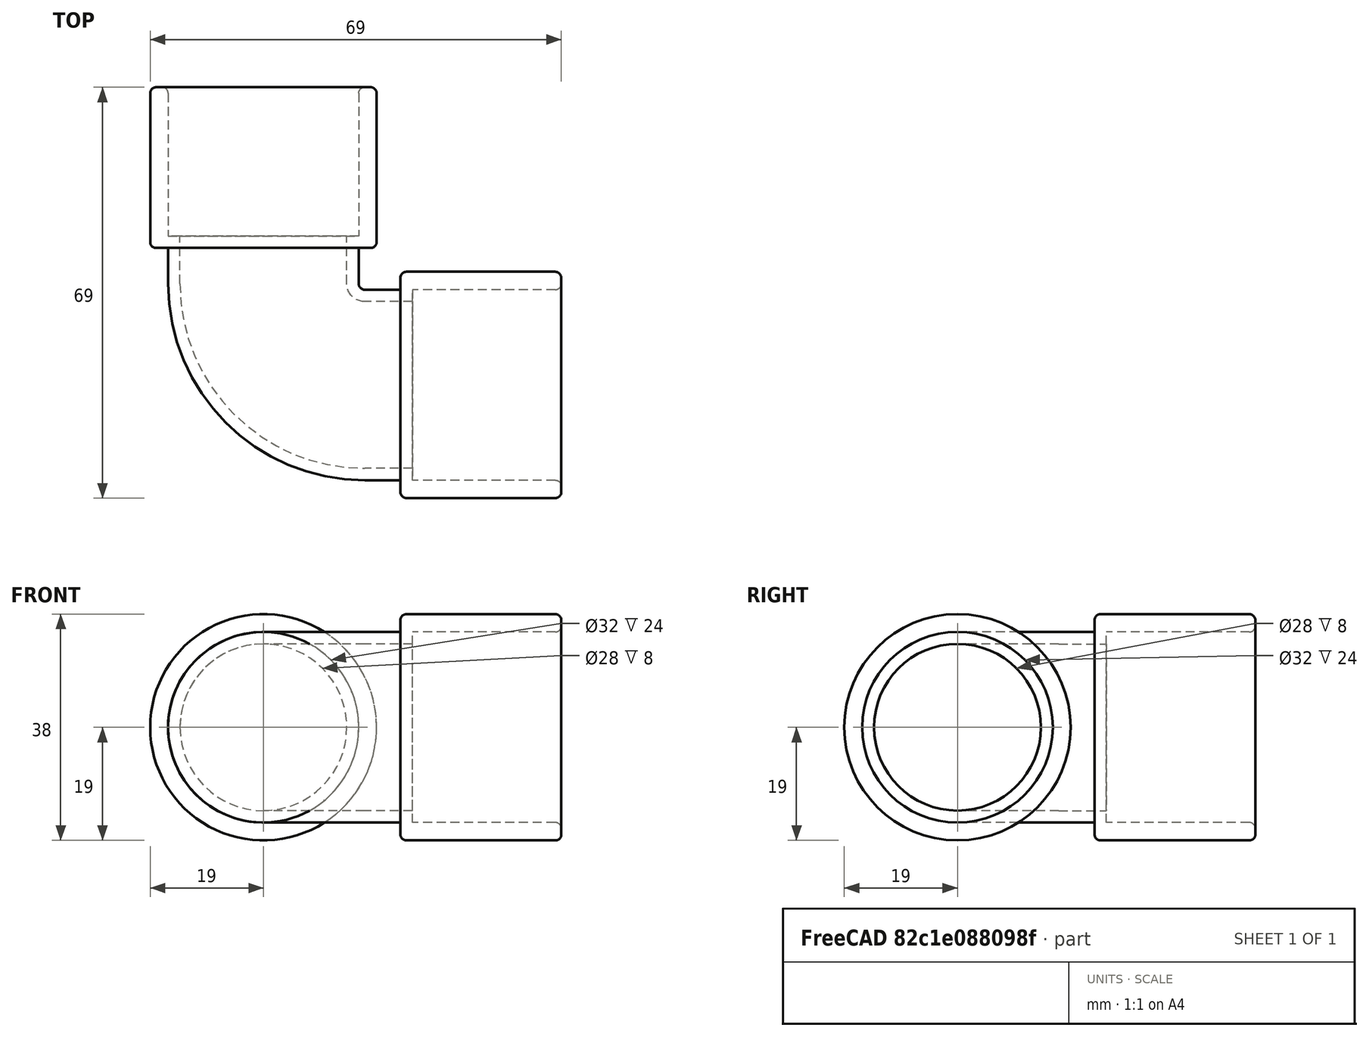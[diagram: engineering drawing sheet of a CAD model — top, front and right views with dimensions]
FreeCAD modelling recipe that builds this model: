
FCSTD DOCUMENT  (FreeCAD 0.16R6706 (Git))
Label: PVC 90º Elbow 32mm
License: CreativeCommons Attribution
LicenseURL: http://creativecommons.org/licenses/by/4.0/
objects: Part::Cylinder×10, Part::Cut×7, Part::Fillet×6, Part::MultiFuse×4, Part::Torus×2
note: 29 computed .brp shape members not serialized (recipe doc carries the construction recipe); baked Part::Feature solids carry a one-line shape summary decoded from their .brp

FEATURE [Part::Cylinder] Cylinder  label="Cilindro"
  Angle = 360
  Height = 6
  Placement = pos=(-6,32,0) rot=(0,1,0;1.5708rad)
  Radius = 16
FEATURE [Part::Cylinder] Cylinder001  label="Cilindro001"
  Angle = 360
  Height = 6
  Placement = pos=(32,0,0) rot=(1,0,0;1.5708rad)
  Radius = 16
FEATURE [Part::Cylinder] Cylinder002  label="Cilindro002"
  Angle = 360
  Height = 27
  Placement = pos=(31,-6,0) rot=(1,0,0;1.5708rad)
  Radius = 19
FEATURE [Part::Cylinder] Cylinder003  label="Cilindro003"
  Angle = 360
  Height = 27
  Placement = pos=(-33,32,0) rot=(0,1,0;1.5708rad)
  Radius = 19
FEATURE [Part::Fillet] Fillet
  Base = -> Cylinder003
  Edges = 1 edges r=1: [Edge1]
FEATURE [Part::Fillet] Fillet001
  Base = -> Cylinder002
  Edges = 1 edges r=1: [Edge3]
FEATURE [Part::Cylinder] Cylinder004  label="Cilindro004"
  Angle = 360
  Height = 26
  Placement = pos=(31,-34,0) rot=(0.57735,-0.57735,-0.57735;4.18879rad)
  Radius = 16
FEATURE [Part::Cylinder] Cylinder005  label="Cilindro005"
  Angle = 360
  Height = 26
  Placement = pos=(-34,32,0) rot=(0,1,0;1.5708rad)
  Radius = 16
FEATURE [Part::Cut] Cut
  Base = -> Fillet
  Tool = -> Cylinder005
FEATURE [Part::Cut] Cut001
  Base = -> Fillet001
  Tool = -> Cylinder004
FEATURE [Part::Cylinder] Cylinder006  label="Cilindro006"
  Angle = 360
  Height = 7
  Placement = pos=(-7,32,0) rot=(0,1,0;1.5708rad)
  Radius = 14
FEATURE [Part::Cut] Cut002
  Base = -> Cylinder
  Placement = pos=(0,1,0) rot=(0,0,1;0rad)
  Tool = -> Cylinder006
FEATURE [Part::Cylinder] Cylinder007  label="Cilindro007"
  Angle = 360
  Height = 4
  Placement = pos=(31,-9,0) rot=(0.57735,-0.57735,-0.57735;4.18879rad)
  Radius = 14
FEATURE [Part::Cut] Cut003
  Base = -> Cut001
  Tool = -> Cylinder007
FEATURE [Part::Cylinder] Cylinder008  label="Cilindro008"
  Angle = 360
  Height = 4
  Placement = pos=(-9,32,0) rot=(0,1,0;1.5708rad)
  Radius = 14
FEATURE [Part::Cut] Cut004
  Base = -> Cut
  Tool = -> Cylinder008
FEATURE [Part::Cylinder] Cylinder009  label="Cilindro009"
  Angle = 360
  Height = 8
  Placement = pos=(32,0,0) rot=(1,0,0;1.5708rad)
  Radius = 14
FEATURE [Part::Cut] Cut005
  Base = -> Cylinder001
  Placement = pos=(1,0,0) rot=(0,0,1;0rad)
  Tool = -> Cylinder009
FEATURE [Part::Torus] Torus001  label="Toro001"
  Angle1 = -180
  Angle2 = 180
  Angle3 = 95
  Placement = pos=(0,0,0) rot=(0,0,-1;0.034907rad)
  Radius1 = 17
  Radius2 = 14
FEATURE [Part::Torus] Torus002  label="Toro002"
  Angle1 = -180
  Angle2 = 180
  Angle3 = 90
  Radius1 = 17
  Radius2 = 16
FEATURE [Part::Cut] Cut006
  Base = -> Torus002
  Tool = -> Torus001
FEATURE [Part::Fillet] Fillet002
  Base = -> Cut003
  Edges = 1 edges r=1: [Edge3]
FEATURE [Part::Fillet] Fillet003
  Base = -> Fillet002
  Edges = 1 edges r=1: [Edge8]
  Placement = pos=(2,0,0) rot=(0,0,1;0rad)
FEATURE [Part::Fillet] Fillet004
  Base = -> Cut004
  Edges = 1 edges r=1: [Edge6]
FEATURE [Part::Fillet] Fillet005
  Base = -> Fillet004
  Edges = 1 edges r=1: [Edge2]
  Placement = pos=(0,1,0) rot=(0,0,1;0rad)
FEATURE [Part::MultiFuse] Fusion
  Placement = pos=(0,-16,0) rot=(0,0,1;0rad)
  Shapes = -> [Cut002,Fillet005]
FEATURE [Part::MultiFuse] Fusion008
  Placement = pos=(-16,0,0) rot=(0,0,1;0rad)
  Shapes = -> [Cut005,Fillet003]
FEATURE [Part::MultiFuse] Fusion009
  Shapes = -> [Fusion,Cut006]
FEATURE [Part::MultiFuse] Fusion010  label="PVC 90º Elbow 32mm"
  Placement = pos=(0,0,0) rot=(0,0,1;3.14159rad)
  Shapes = -> [Fusion008,Fusion009]
